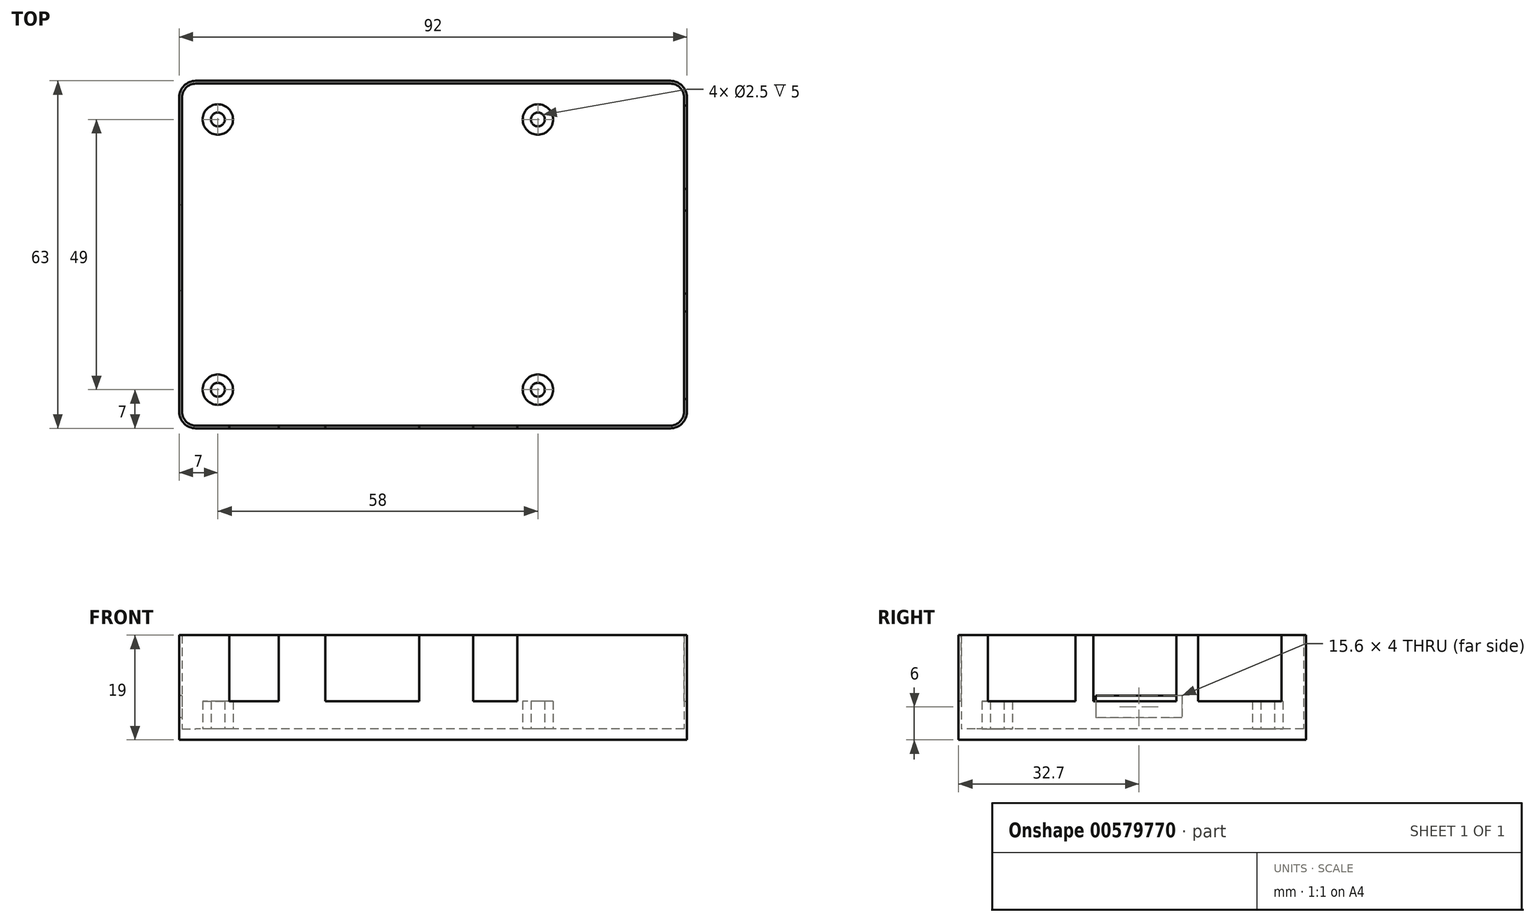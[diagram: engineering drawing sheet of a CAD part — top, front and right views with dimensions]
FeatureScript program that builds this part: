
annotation { "Feature Type Name" : "Feature", "Feature Type Description" : "" }
export const myFeature = defineFeature(function(context is Context, id is Id, definition is map)
    precondition{}
    {
        {
            var Q0;
            Q0=qCreatedBy(makeId("Top.planeOp"),FACE);
            var sketch = newSketch(context, id + "F0", { "sketchPlane" : qUnion([Q0])});
            skLineSegment(sketch, "E0.bottom", {"start": v(2.5, 0) * mm, "end": v(88.5, 0) * mm});
            skLineSegment(sketch, "E0.top", {"start": v(2.5, 62) * mm, "end": v(88.5, 62) * mm});
            skLineSegment(sketch, "E0.left", {"start": v(0, 2.5) * mm, "end": v(0, 59.5) * mm});
            skLineSegment(sketch, "E0.right", {"start": v(91, 2.5) * mm, "end": v(91, 59.5) * mm});
            skPoint(sketch, "E1.visualSharp", {"position": v(0, 62) * mm});
            skArc(sketch, "E1.filletArc", {"start": v(2.5, 62) * mm, "mid": v(0.73, 61.27) * mm, "end": v(0, 59.5) * mm});
            skPoint(sketch, "E2.visualSharp", {"position": v(0, 0) * mm});
            skArc(sketch, "E2.filletArc", {"start": v(0, 2.5) * mm, "mid": v(0.73, 0.73) * mm, "end": v(2.5, 0) * mm});
            skPoint(sketch, "E3.visualSharp", {"position": v(91, 0) * mm});
            skArc(sketch, "E3.filletArc", {"start": v(88.5, 0) * mm, "mid": v(90.27, 0.73) * mm, "end": v(91, 2.5) * mm});
            skPoint(sketch, "E4.visualSharp", {"position": v(91, 62) * mm});
            skArc(sketch, "E4.filletArc", {"start": v(91, 59.5) * mm, "mid": v(90.27, 61.27) * mm, "end": v(88.5, 62) * mm});
            skLineSegment(sketch, "E5.0", {"start": v(2.5, 62.5) * mm, "end": v(88.5, 62.5) * mm});
            skArc(sketch, "E5.1", {"start": v(91.5, 59.5) * mm, "mid": v(90.62, 61.62) * mm, "end": v(88.5, 62.5) * mm});
            skArc(sketch, "E5.2", {"start": v(2.5, 62.5) * mm, "mid": v(0.38, 61.62) * mm, "end": v(-0.5, 59.5) * mm});
            skLineSegment(sketch, "E5.3", {"start": v(91.5, 2.5) * mm, "end": v(91.5, 59.5) * mm});
            skLineSegment(sketch, "E5.4", {"start": v(-0.5, 2.5) * mm, "end": v(-0.5, 59.5) * mm});
            skArc(sketch, "E5.5", {"start": v(-0.5, 2.5) * mm, "mid": v(0.38, 0.38) * mm, "end": v(2.5, -0.5) * mm});
            skLineSegment(sketch, "E5.6", {"start": v(2.5, -0.5) * mm, "end": v(88.5, -0.5) * mm});
            skArc(sketch, "E5.7", {"start": v(88.5, -0.5) * mm, "mid": v(90.62, 0.38) * mm, "end": v(91.5, 2.5) * mm});
            skSolve(sketch);
        }
        {
            var Q0;
            Q0=makeQuery(id+"F0.imprint","IMPRINT",FACE,{"disambiguationData":[TD([[makeQuery(id+"F0.imprint","IMPRINT",EDGE,{"derivedFrom":sQuery(id+"F0.wireOp",EDGE,"E0.bottom")}),1.0]])]});
            var Q1;
            Q1=makeQuery(id+"F0.imprint","IMPRINT",FACE,{"disambiguationData":[TD([[makeQuery(id+"F0.imprint","IMPRINT",EDGE,{"derivedFrom":sQuery(id+"F0.wireOp",EDGE,"E0.bottom")}),-1.0]])]});
            extrude(context, id + "F1", {"entities" : qUnion([Q0, Q1]), "depth" : 2 * mm, "offsetDistance" : 25 * mm});
        }
        {
            var Q0;
            Q0 = qSketchRegion(id + "F0", true);
            extrude(context, id + "F2", {"entities" : qUnion([Q0]), "operationType" : NewBodyOperationType.ADD, "depth" : 19 * mm, "offsetDistance" : 25 * mm});
        }
        {
            var Q0;
            Q0=makeQuery(id+"F1.opExtrude","CAP_FACE",FACE,{"disambiguationData":[OSD([sQuery(id+"F0.wireOp",EDGE,"E5.0"),sQuery(id+"F0.wireOp",EDGE,"E5.1"),sQuery(id+"F0.wireOp",EDGE,"E5.2"),sQuery(id+"F0.wireOp",EDGE,"E5.3"),sQuery(id+"F0.wireOp",EDGE,"E5.4"),sQuery(id+"F0.wireOp",EDGE,"E5.5"),sQuery(id+"F0.wireOp",EDGE,"E5.6"),sQuery(id+"F0.wireOp",EDGE,"E5.7")])],"isStart":false});
            var sketch = newSketch(context, id + "F3", { "sketchPlane" : qUnion([Q0])});
            skCircle(sketch, "E6", {"center": v(6.5, 55.5) * mm, "radius": 2.75 * mm});
            skCircle(sketch, "E7", {"center": v(64.5, 55.5) * mm, "radius": 2.75 * mm});
            skCircle(sketch, "E8", {"center": v(6.5, 6.5) * mm, "radius": 2.75 * mm});
            skCircle(sketch, "E9", {"center": v(64.5, 6.5) * mm, "radius": 2.75 * mm});
            skCircle(sketch, "E10", {"center": v(6.5, 55.5) * mm, "radius": 1.25 * mm});
            skCircle(sketch, "E11", {"center": v(64.5, 55.5) * mm, "radius": 1.25 * mm});
            skCircle(sketch, "E12", {"center": v(64.5, 6.5) * mm, "radius": 1.25 * mm});
            skCircle(sketch, "E13", {"center": v(6.5, 6.5) * mm, "radius": 1.25 * mm});
            skSolve(sketch);
        }
        {
            var Q0;
            Q0 = qSketchRegion(id + "F3", true);
            extrude(context, id + "F4", {"entities" : qUnion([Q0]), "operationType" : NewBodyOperationType.ADD, "depth" : 5 * mm, "offsetDistance" : 25 * mm});
        }
        {
            var Q0;
            Q0=makeQuery(id+"F2.opExtrude","CAP_FACE",FACE,{"disambiguationData":[OSD([sQuery(id+"F0.wireOp",EDGE,"E0.bottom"),sQuery(id+"F0.wireOp",EDGE,"E0.top"),sQuery(id+"F0.wireOp",EDGE,"E0.left"),sQuery(id+"F0.wireOp",EDGE,"E0.right"),sQuery(id+"F0.wireOp",EDGE,"E1.filletArc"),sQuery(id+"F0.wireOp",EDGE,"E2.filletArc"),sQuery(id+"F0.wireOp",EDGE,"E3.filletArc"),sQuery(id+"F0.wireOp",EDGE,"E4.filletArc"),sQuery(id+"F0.wireOp",EDGE,"E5.0"),sQuery(id+"F0.wireOp",EDGE,"E5.1"),sQuery(id+"F0.wireOp",EDGE,"E5.2"),sQuery(id+"F0.wireOp",EDGE,"E5.3"),sQuery(id+"F0.wireOp",EDGE,"E5.4"),sQuery(id+"F0.wireOp",EDGE,"E5.5"),sQuery(id+"F0.wireOp",EDGE,"E5.6"),sQuery(id+"F0.wireOp",EDGE,"E5.7")])],"isStart":false});
            var sketch = newSketch(context, id + "F5", { "sketchPlane" : qUnion([Q0])});
            skLineSegment(sketch, "E14.bottom", {"start": v(8.55, 0) * mm, "end": v(17.55, 0) * mm});
            skLineSegment(sketch, "E14.top", {"start": v(8.55, -0.5) * mm, "end": v(17.55, -0.5) * mm});
            skLineSegment(sketch, "E14.left", {"start": v(8.55, 0) * mm, "end": v(8.55, -0.5) * mm});
            skLineSegment(sketch, "E14.right", {"start": v(17.55, 0) * mm, "end": v(17.55, -0.5) * mm});
            skLineSegment(sketch, "E15.bottom", {"start": v(26, 0) * mm, "end": v(43, 0) * mm});
            skLineSegment(sketch, "E15.top", {"start": v(26, -0.5) * mm, "end": v(43, -0.5) * mm});
            skLineSegment(sketch, "E15.left", {"start": v(26, 0) * mm, "end": v(26, -0.5) * mm});
            skLineSegment(sketch, "E15.right", {"start": v(43, 0) * mm, "end": v(43, -0.5) * mm});
            skLineSegment(sketch, "E16.bottom", {"start": v(52.75, 0) * mm, "end": v(60.75, 0) * mm});
            skLineSegment(sketch, "E16.top", {"start": v(52.75, -0.5) * mm, "end": v(60.75, -0.5) * mm});
            skLineSegment(sketch, "E16.left", {"start": v(52.75, 0) * mm, "end": v(52.75, -0.5) * mm});
            skLineSegment(sketch, "E16.right", {"start": v(60.75, 0) * mm, "end": v(60.75, -0.5) * mm});
            skLineSegment(sketch, "E17.bottom", {"start": v(91, 58) * mm, "end": v(91.5, 58) * mm});
            skLineSegment(sketch, "E17.top", {"start": v(91, 42.9) * mm, "end": v(91.5, 42.9) * mm});
            skLineSegment(sketch, "E17.left", {"start": v(91, 58) * mm, "end": v(91, 42.9) * mm});
            skLineSegment(sketch, "E17.right", {"start": v(91.5, 58) * mm, "end": v(91.5, 42.9) * mm});
            skLineSegment(sketch, "E18.bottom", {"start": v(91, 39) * mm, "end": v(91.5, 39) * mm});
            skLineSegment(sketch, "E18.top", {"start": v(91, 23.9) * mm, "end": v(91.5, 23.9) * mm});
            skLineSegment(sketch, "E18.left", {"start": v(91, 39) * mm, "end": v(91, 23.9) * mm});
            skLineSegment(sketch, "E18.right", {"start": v(91.5, 39) * mm, "end": v(91.5, 23.9) * mm});
            skLineSegment(sketch, "E19.bottom", {"start": v(91, 20.7) * mm, "end": v(91.5, 20.7) * mm});
            skLineSegment(sketch, "E19.top", {"start": v(91, 4.8) * mm, "end": v(91.5, 4.8) * mm});
            skLineSegment(sketch, "E19.left", {"start": v(91, 20.7) * mm, "end": v(91, 4.8) * mm});
            skLineSegment(sketch, "E19.right", {"start": v(91.5, 20.7) * mm, "end": v(91.5, 4.8) * mm});
            skSolve(sketch);
        }
        {
            var Q0;
            Q0 = qSketchRegion(id + "F5", true);
            extrude(context, id + "F6", {"entities" : qUnion([Q0]), "operationType" : NewBodyOperationType.REMOVE, "oppositeDirection" : true, "depth" : 12 * mm, "offsetDistance" : 25 * mm});
        }
        {
            var Q0;
            {var subQ0=sQuery(id+"F0.wireOp",EDGE,"E5.4");Q0=makeQuery(id+"F2.boolean.opBoolean","MERGE",FACE,{"derivedFrom":[makeQuery(id+"F1.opExtrude","SWEPT_FACE",FACE,{"disambiguationData":[OSD([subQ0])]}),makeQuery(id+"F2.opExtrude","SWEPT_FACE",FACE,{"disambiguationData":[OSD([subQ0])]})]});}
            var sketch = newSketch(context, id + "F7", { "sketchPlane" : qUnion([Q0])});
            skLineSegment(sketch, "E20.bottom", {"start": v(-40, 8) * mm, "end": v(-24.4, 8) * mm});
            skLineSegment(sketch, "E20.top", {"start": v(-40, 4) * mm, "end": v(-24.4, 4) * mm});
            skLineSegment(sketch, "E20.left", {"start": v(-40, 8) * mm, "end": v(-40, 4) * mm});
            skLineSegment(sketch, "E20.right", {"start": v(-24.4, 8) * mm, "end": v(-24.4, 4) * mm});
            skSolve(sketch);
        }
        {
            var Q0;
            Q0=makeQuery(id+"F7.imprint","IMPRINT",FACE,{"disambiguationData":[TD([[makeQuery(id+"F7.imprint","IMPRINT",EDGE,{"derivedFrom":sQuery(id+"F7.wireOp",EDGE,"E20.bottom")}),-1.0]])]});
            extrude(context, id + "F8", {"entities" : qUnion([Q0]), "operationType" : NewBodyOperationType.REMOVE, "oppositeDirection" : true, "depth" : 0.5 * mm, "offsetDistance" : 25 * mm});
        }
    });
